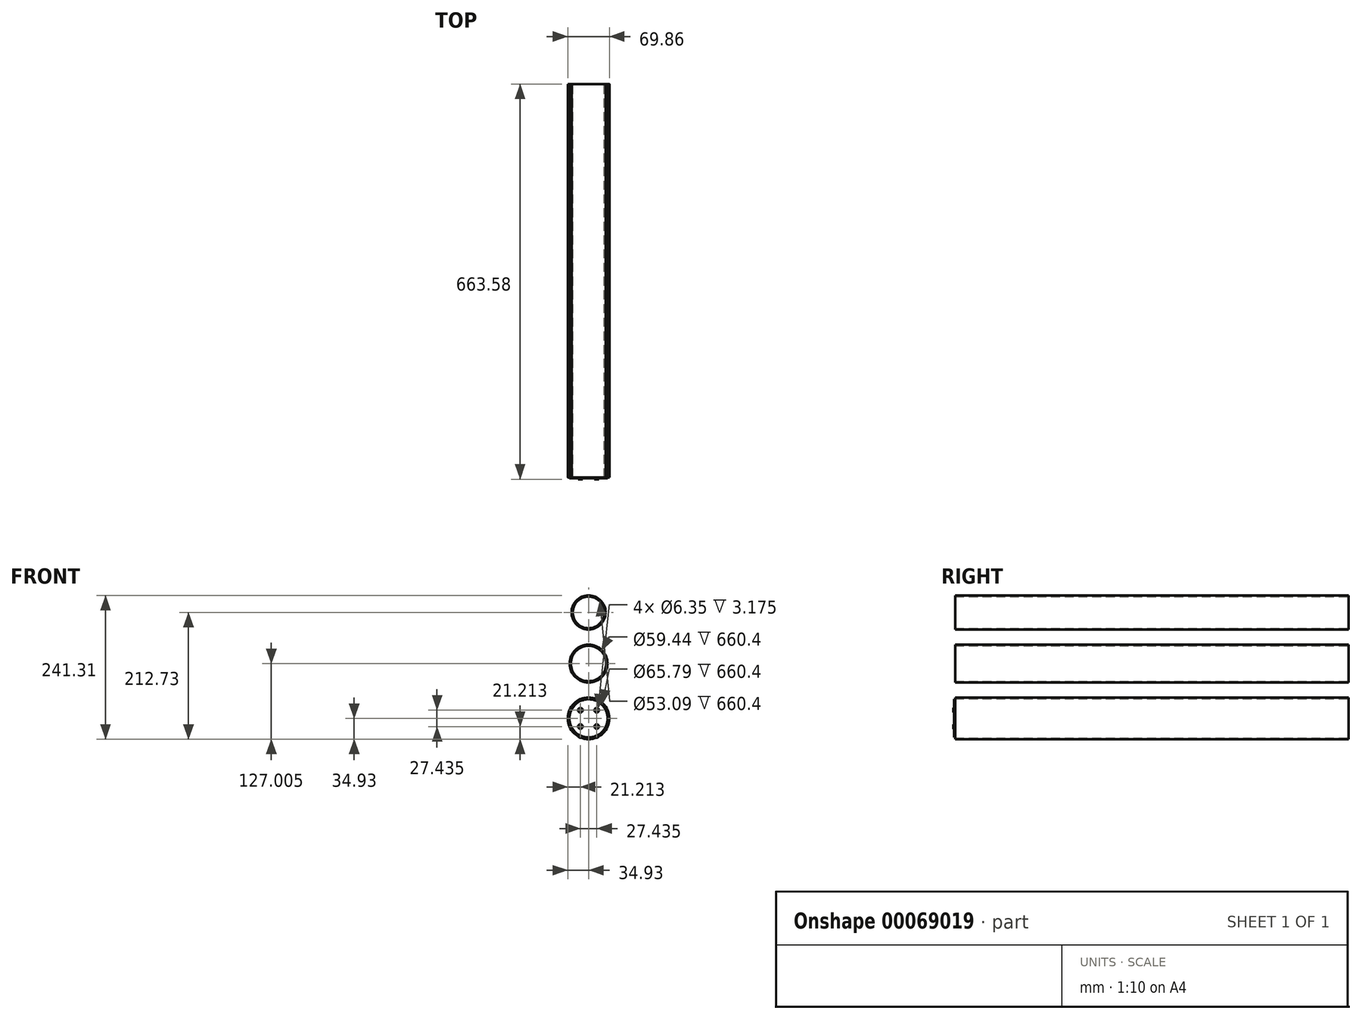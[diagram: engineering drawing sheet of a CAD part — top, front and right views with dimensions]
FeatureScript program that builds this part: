
annotation { "Feature Type Name" : "Feature", "Feature Type Description" : "" }
export const myFeature = defineFeature(function(context is Context, id is Id, definition is map)
    precondition{}
    {
        {
            var Q0;
            Q0=qCreatedBy(makeId("Front.planeOp"),FACE);
            var sketch = newSketch(context, id + "F0", { "sketchPlane" : qUnion([Q0])});
            skCircle(sketch, "E0", {"center": v(0, 0) * mm, "radius": 34.93 * mm});
            skCircle(sketch, "E1", {"center": v(0, 92.08) * mm, "radius": 31.75 * mm});
            skCircle(sketch, "E2", {"center": v(0, 177.8) * mm, "radius": 28.58 * mm});
            skCircle(sketch, "E3", {"center": v(0, 177.8) * mm, "radius": 26.54 * mm});
            skCircle(sketch, "E4", {"center": v(0, 92.08) * mm, "radius": 29.72 * mm});
            skCircle(sketch, "E5", {"center": v(0, 0) * mm, "radius": 32.9 * mm});
            skSolve(sketch);
        }
        {
            var Q0;
            Q0=makeQuery(id+"F0.imprint","IMPRINT",FACE,{"disambiguationData":[TD([[makeQuery(id+"F0.imprint","IMPRINT",EDGE,{"derivedFrom":sQuery(id+"F0.wireOp",EDGE,"E2")}),1.0]])]});
            var Q1;
            Q1=makeQuery(id+"F0.imprint","IMPRINT",FACE,{"disambiguationData":[TD([[makeQuery(id+"F0.imprint","IMPRINT",EDGE,{"derivedFrom":sQuery(id+"F0.wireOp",EDGE,"E1")}),1.0]])]});
            var Q2;
            Q2=makeQuery(id+"F0.imprint","IMPRINT",FACE,{"disambiguationData":[TD([[makeQuery(id+"F0.imprint","IMPRINT",EDGE,{"derivedFrom":sQuery(id+"F0.wireOp",EDGE,"E0")}),1.0]])]});
            extrude(context, id + "F1", {"entities" : qUnion([Q0, Q1, Q2]), "depth" : 660.4 * mm});
        }
        {
            var Q0;
            Q0=makeQuery(id+"F1.opExtrude","CAP_FACE",FACE,{"disambiguationData":[OSD([sQuery(id+"F0.wireOp",EDGE,"E0"),sQuery(id+"F0.wireOp",EDGE,"E5")])],"isStart":false});
            var sketch = newSketch(context, id + "F2", { "sketchPlane" : qUnion([Q0])});
            skCircle(sketch, "E6.0", {"center": v(0, 0) * mm, "radius": 32.9 * mm});
            skCircle(sketch, "E7", {"center": v(0, 0) * mm, "radius": 32.1 * mm});
            skSolve(sketch);
        }
        {
            var Q0;
            Q0=makeQuery(id+"F2.imprint","IMPRINT",FACE,{"disambiguationData":[TD([[makeQuery(id+"F2.imprint","IMPRINT",EDGE,{"derivedFrom":sQuery(id+"F2.wireOp",EDGE,"E7")}),1.0]])]});
            extrude(context, id + "F3", {"entities" : qUnion([Q0]), "depth" : 1.59 * mm});
        }
        {
            var Q0;
            Q0=makeQuery(id+"F3.opExtrude","CAP_FACE",FACE,{"disambiguationData":[OSD([sQuery(id+"F2.wireOp",EDGE,"E7")])],"isStart":false});
            var sketch = newSketch(context, id + "F4", { "sketchPlane" : qUnion([Q0])});
            skCircle(sketch, "E8", {"center": v(0, 0) * mm, "radius": 19.4 * mm, "construction": true});
            skCircle(sketch, "E9", {"center": v(13.72, 13.72) * mm, "radius": 3.81 * mm});
            skCircle(sketch, "E10", {"center": v(13.72, 13.72) * mm, "radius": 3.18 * mm});
            skCircle(sketch, "E11.1.0", {"center": v(-13.72, 13.72) * mm, "radius": 3.81 * mm});
            skCircle(sketch, "E11.1.1", {"center": v(-13.72, 13.72) * mm, "radius": 3.18 * mm});
            skCircle(sketch, "E11.2.0", {"center": v(-13.72, -13.72) * mm, "radius": 3.81 * mm});
            skCircle(sketch, "E11.2.1", {"center": v(-13.72, -13.72) * mm, "radius": 3.18 * mm});
            skCircle(sketch, "E11.3.0", {"center": v(13.72, -13.72) * mm, "radius": 3.81 * mm});
            skCircle(sketch, "E11.3.1", {"center": v(13.72, -13.72) * mm, "radius": 3.18 * mm});
            skLineSegment(sketch, "E12", {"start": v(0, 0) * mm, "end": v(0, 48.97) * mm, "construction": true});
            skLineSegment(sketch, "E13", {"start": v(0, 48.97) * mm, "end": v(0, 0) * mm, "construction": true});
            skLineSegment(sketch, "E14", {"start": v(72.75, 0) * mm, "end": v(0, 0) * mm, "construction": true});
            skLineSegment(sketch, "E15", {"start": v(0, 0) * mm, "end": v(13.72, 13.72) * mm, "construction": true});
            skSolve(sketch);
        }
        {
            var Q0;
            Q0=makeQuery(id+"F4.imprint","IMPRINT",FACE,{"disambiguationData":[TD([[makeQuery(id+"F4.imprint","IMPRINT",EDGE,{"derivedFrom":sQuery(id+"F4.wireOp",EDGE,"E11.1.0")}),1.0]])]});
            var Q1;
            Q1=makeQuery(id+"F4.imprint","IMPRINT",FACE,{"disambiguationData":[TD([[makeQuery(id+"F4.imprint","IMPRINT",EDGE,{"derivedFrom":sQuery(id+"F4.wireOp",EDGE,"E9")}),1.0]])]});
            var Q2;
            Q2=makeQuery(id+"F4.imprint","IMPRINT",FACE,{"disambiguationData":[TD([[makeQuery(id+"F4.imprint","IMPRINT",EDGE,{"derivedFrom":sQuery(id+"F4.wireOp",EDGE,"E11.3.0")}),1.0]])]});
            var Q3;
            Q3=makeQuery(id+"F4.imprint","IMPRINT",FACE,{"disambiguationData":[TD([[makeQuery(id+"F4.imprint","IMPRINT",EDGE,{"derivedFrom":sQuery(id+"F4.wireOp",EDGE,"E11.2.0")}),1.0]])]});
            extrude(context, id + "F5", {"entities" : qUnion([Q0, Q1, Q2, Q3]), "operationType" : NewBodyOperationType.ADD, "depth" : 1.59 * mm});
        }
        {
            var Q0;
            Q0=makeQuery(id+"F4.imprint","IMPRINT",FACE,{"disambiguationData":[TD([[makeQuery(id+"F4.imprint","IMPRINT",EDGE,{"derivedFrom":sQuery(id+"F4.wireOp",EDGE,"E11.1.1")}),1.0]])]});
            var Q1;
            Q1=makeQuery(id+"F4.imprint","IMPRINT",FACE,{"disambiguationData":[TD([[makeQuery(id+"F4.imprint","IMPRINT",EDGE,{"derivedFrom":sQuery(id+"F4.wireOp",EDGE,"E10")}),1.0]])]});
            var Q2;
            Q2=makeQuery(id+"F4.imprint","IMPRINT",FACE,{"disambiguationData":[TD([[makeQuery(id+"F4.imprint","IMPRINT",EDGE,{"derivedFrom":sQuery(id+"F4.wireOp",EDGE,"E11.3.1")}),1.0]])]});
            var Q3;
            Q3=makeQuery(id+"F4.imprint","IMPRINT",FACE,{"disambiguationData":[TD([[makeQuery(id+"F4.imprint","IMPRINT",EDGE,{"derivedFrom":sQuery(id+"F4.wireOp",EDGE,"E11.2.1")}),1.0]])]});
            extrude(context, id + "F6", {"entities" : qUnion([Q0, Q1, Q2, Q3]), "operationType" : NewBodyOperationType.REMOVE, "endBound" : BoundingType.THROUGH_ALL, "oppositeDirection" : true, "depth" : 25.4 * mm});
        }
    });
